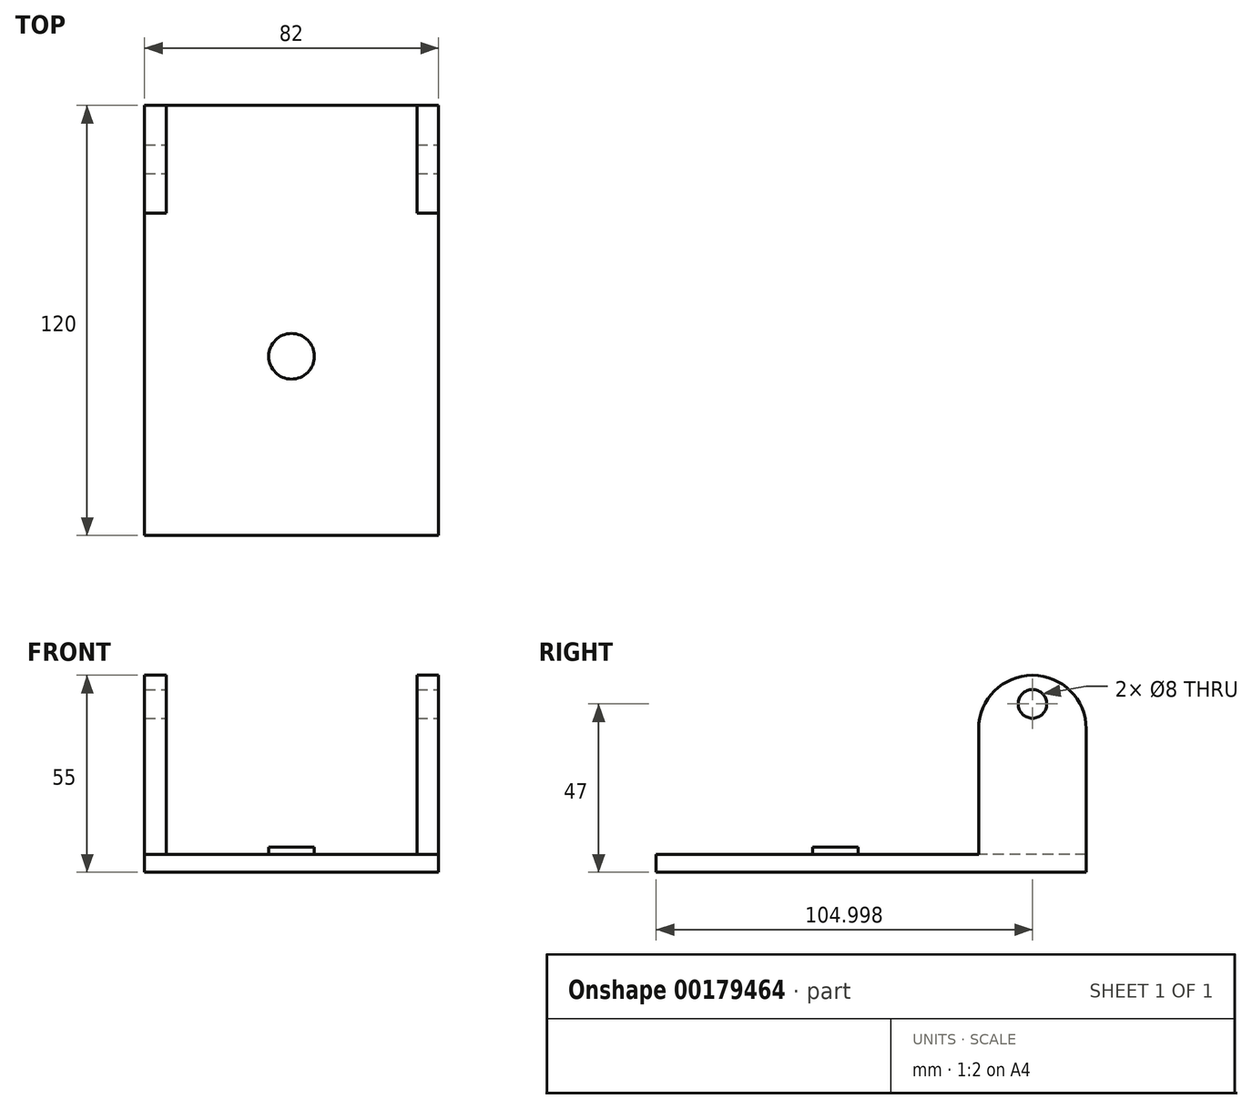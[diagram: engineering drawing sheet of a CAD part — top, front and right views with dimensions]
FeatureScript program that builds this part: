
annotation { "Feature Type Name" : "Feature", "Feature Type Description" : "" }
export const myFeature = defineFeature(function(context is Context, id is Id, definition is map)
    precondition{}
    {
        {
            var Q0;
            Q0=qCreatedBy(makeId("Top.planeOp"),FACE);
            var sketch = newSketch(context, id + "F0", { "sketchPlane" : qUnion([Q0])});
            skLineSegment(sketch, "E0.bottom", {"start": v(39.08, -59.83) * mm, "end": v(-42.92, -59.83) * mm});
            skLineSegment(sketch, "E0.top", {"start": v(39.08, 60.17) * mm, "end": v(-42.92, 60.17) * mm});
            skLineSegment(sketch, "E0.left", {"start": v(39.08, -59.83) * mm, "end": v(39.08, 60.17) * mm});
            skLineSegment(sketch, "E0.right", {"start": v(-42.92, -59.83) * mm, "end": v(-42.92, 60.17) * mm});
            skPoint(sketch, "E0.middle", {"position": v(-1.92, 0.17) * mm});
            skSolve(sketch);
        }
        {
            var Q0;
            Q0=makeQuery(id+"F0.imprint","IMPRINT",FACE,{"disambiguationData":[TD([[makeQuery(id+"F0.imprint","IMPRINT",EDGE,{"derivedFrom":sQuery(id+"F0.wireOp",EDGE,"E0.bottom")}),-1.0]])]});
            extrude(context, id + "F1", {"entities" : qUnion([Q0]), "depth" : 5 * mm});
        }
        {
            var Q0;
            Q0=makeQuery(id+"F1.opExtrude","CAP_FACE",FACE,{"disambiguationData":[OSD([sQuery(id+"F0.wireOp",EDGE,"E0.bottom"),sQuery(id+"F0.wireOp",EDGE,"E0.top"),sQuery(id+"F0.wireOp",EDGE,"E0.left"),sQuery(id+"F0.wireOp",EDGE,"E0.right")])],"isStart":false});
            var sketch = newSketch(context, id + "F2", { "sketchPlane" : qUnion([Q0])});
            skCircle(sketch, "E1", {"center": v(-1.92, -9.83) * mm, "radius": 6.38 * mm});
            skLineSegment(sketch, "E2", {"start": v(-1.92, -59.83) * mm, "end": v(-1.92, -9.83) * mm});
            skSolve(sketch);
        }
        {
            var Q0;
            Q0=makeQuery(id+"F2.imprint","IMPRINT",FACE,{"disambiguationData":[TD([[makeQuery(id+"F2.imprint","IMPRINT",EDGE,{"derivedFrom":sQuery(id+"F2.wireOp",EDGE,"E1")}),1.0]])]});
            extrude(context, id + "F3", {"entities" : qUnion([Q0]), "operationType" : NewBodyOperationType.ADD, "depth" : 2 * mm});
        }
        {
            var Q0;
            Q0=makeQuery(id+"F1.opExtrude","CAP_FACE",FACE,{"disambiguationData":[OSD([sQuery(id+"F0.wireOp",EDGE,"E0.bottom"),sQuery(id+"F0.wireOp",EDGE,"E0.top"),sQuery(id+"F0.wireOp",EDGE,"E0.left"),sQuery(id+"F0.wireOp",EDGE,"E0.right")])],"isStart":false});
            var sketch = newSketch(context, id + "F4", { "sketchPlane" : qUnion([Q0])});
            skLineSegment(sketch, "E3.bottom", {"start": v(-42.92, 60.17) * mm, "end": v(-36.92, 60.17) * mm});
            skLineSegment(sketch, "E3.top", {"start": v(-42.92, 30.17) * mm, "end": v(-36.92, 30.17) * mm});
            skLineSegment(sketch, "E3.left", {"start": v(-42.92, 60.17) * mm, "end": v(-42.92, 30.17) * mm});
            skLineSegment(sketch, "E3.right", {"start": v(-36.92, 60.17) * mm, "end": v(-36.92, 30.17) * mm});
            skLineSegment(sketch, "E4.bottom", {"start": v(39.08, 60.17) * mm, "end": v(33.08, 60.17) * mm});
            skLineSegment(sketch, "E4.top", {"start": v(39.08, 30.17) * mm, "end": v(33.08, 30.17) * mm});
            skLineSegment(sketch, "E4.left", {"start": v(39.08, 60.17) * mm, "end": v(39.08, 30.17) * mm});
            skLineSegment(sketch, "E4.right", {"start": v(33.08, 60.17) * mm, "end": v(33.08, 30.17) * mm});
            skSolve(sketch);
        }
        {
            var Q0;
            Q0=makeQuery(id+"F4.imprint","IMPRINT",FACE,{"disambiguationData":[TD([[makeQuery(id+"F4.imprint","IMPRINT",EDGE,{"derivedFrom":sQuery(id+"F4.wireOp",EDGE,"E3.bottom")}),1.0]])]});
            var Q1;
            Q1=makeQuery(id+"F4.imprint","IMPRINT",FACE,{"disambiguationData":[TD([[makeQuery(id+"F4.imprint","IMPRINT",EDGE,{"derivedFrom":sQuery(id+"F4.wireOp",EDGE,"E4.bottom")}),1.0]])]});
            extrude(context, id + "F5", {"entities" : qUnion([Q0, Q1]), "operationType" : NewBodyOperationType.ADD, "depth" : 50 * mm});
        }
        {
            var Q0;
            Q0=makeQuery(id+"F5.boolean.opBoolean","MERGE",FACE,{"derivedFrom":[makeQuery(id+"F1.opExtrude","SWEPT_FACE",FACE,{"disambiguationData":[OSD([sQuery(id+"F0.wireOp",EDGE,"E0.left")])]}),makeQuery(id+"F5.opExtrude","SWEPT_FACE",FACE,{"disambiguationData":[OSD([sQuery(id+"F4.wireOp",EDGE,"E4.left")])]})]});
            var sketch = newSketch(context, id + "F6", { "sketchPlane" : qUnion([Q0])});
            skCircle(sketch, "E5", {"center": v(45.17, 47) * mm, "radius": 4 * mm});
            skLineSegment(sketch, "E6", {"start": v(45.17, 55) * mm, "end": v(45.17, 8.9) * mm});
            skSolve(sketch);
        }
        {
            var Q0;
            Q0=makeQuery(id+"F6.imprint","IMPRINT",FACE,{"disambiguationData":[TD([[makeQuery(id+"F6.imprint","IMPRINT",EDGE,{"derivedFrom":sQuery(id+"F6.wireOp",EDGE,"E5")}),1.0]])]});
            extrude(context, id + "F7", {"entities" : qUnion([Q0]), "operationType" : NewBodyOperationType.REMOVE, "endBound" : BoundingType.THROUGH_ALL, "oppositeDirection" : true, "depth" : 25 * mm});
        }
        {
            var Q0;
            Q0=makeQuery(id+"F5.opExtrude","CAP_EDGE",EDGE,{"disambiguationData":[OSD([sQuery(id+"F4.wireOp",EDGE,"E4.top")])],"isStart":false});
            var Q1;
            Q1=makeQuery(id+"F5.opExtrude","CAP_EDGE",EDGE,{"disambiguationData":[OSD([sQuery(id+"F4.wireOp",EDGE,"E3.top")])],"isStart":false});
            var Q2;
            Q2=makeQuery(id+"F5.opExtrude","CAP_EDGE",EDGE,{"disambiguationData":[OSD([sQuery(id+"F4.wireOp",EDGE,"E3.bottom")])],"isStart":false});
            var Q3;
            Q3=makeQuery(id+"F5.opExtrude","CAP_EDGE",EDGE,{"disambiguationData":[OSD([sQuery(id+"F4.wireOp",EDGE,"E4.bottom")])],"isStart":false});
            fillet(context, id + "F8", {"entities" : qUnion([Q0, Q1, Q2, Q3]), "radius" : 15 * mm, "tangentPropagation" : true, "allowEdgeOverflow" : false});
        }
    });
